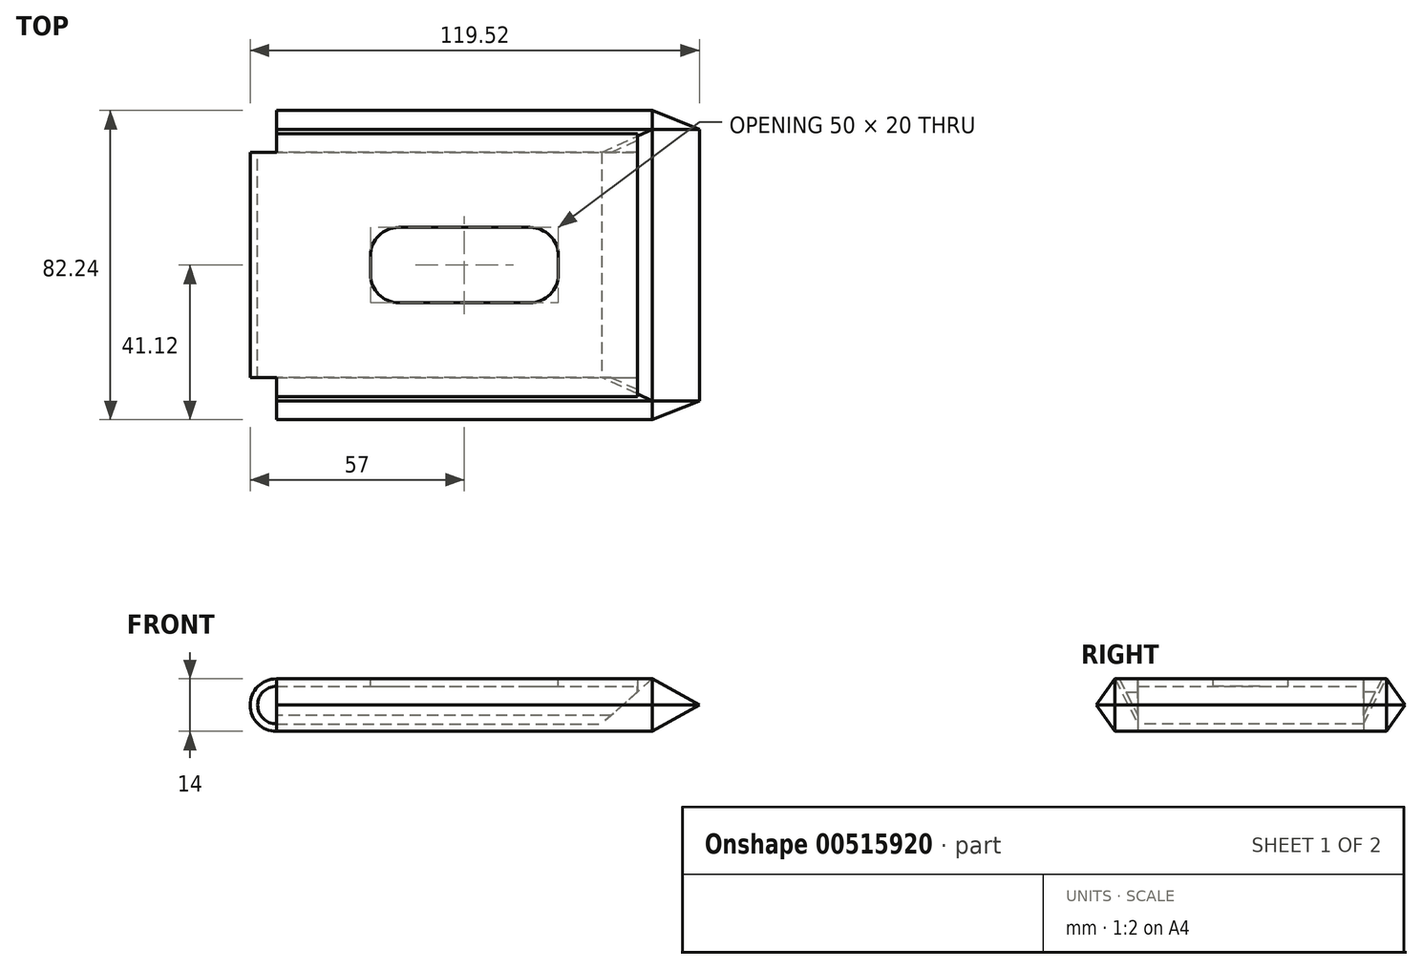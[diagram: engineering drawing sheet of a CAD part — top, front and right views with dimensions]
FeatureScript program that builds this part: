
annotation { "Feature Type Name" : "Feature", "Feature Type Description" : "" }
export const myFeature = defineFeature(function(context is Context, id is Id, definition is map)
    precondition{}
    {
        {
            var Q0;
            Q0=qCreatedBy(makeId("Front.planeOp"),FACE);
            var sketch = newSketch(context, id + "F0", { "sketchPlane" : qUnion([Q0])});
            skArc(sketch, "E0", {"start": v(0, 5) * mm, "mid": v(-5, 0) * mm, "end": v(0, -5) * mm});
            skLineSegment(sketch, "E1", {"start": v(0, 5) * mm, "end": v(100, 5) * mm});
            skLineSegment(sketch, "E2", {"start": v(0, -5) * mm, "end": v(100, -5) * mm});
            skLineSegment(sketch, "E3.0", {"start": v(0, 7) * mm, "end": v(100, 7) * mm});
            skArc(sketch, "E3.1", {"start": v(0, 7) * mm, "mid": v(-7, 0) * mm, "end": v(0, -7) * mm});
            skLineSegment(sketch, "E3.2", {"start": v(0, -7) * mm, "end": v(100, -7) * mm});
            skLineSegment(sketch, "E4", {"start": v(100, 7) * mm, "end": v(100, 5) * mm});
            skLineSegment(sketch, "E5", {"start": v(100, -5) * mm, "end": v(100, -7) * mm});
            skSolve(sketch);
        }
        {
            var Q0;
            Q0 = qSketchRegion(id + "F0", true);
            extrude(context, id + "F1", {"entities" : qUnion([Q0]), "depth" : 60 * mm, "offsetDistance" : 25 * mm});
        }
        {
            var Q0;
            Q0=makeQuery(id+"F1.opExtrude","SWEPT_FACE",FACE,{"disambiguationData":[OSD([sQuery(id+"F0.wireOp",EDGE,"E3.0")])]});
            var sketch = newSketch(context, id + "F2", { "sketchPlane" : qUnion([Q0])});
            skLineSegment(sketch, "E6", {"start": v(50, 0) * mm, "end": v(50, -60) * mm, "construction": true});
            skLineSegment(sketch, "E7.bottom", {"start": v(67.5, -40) * mm, "end": v(32.5, -40) * mm});
            skLineSegment(sketch, "E7.top", {"start": v(67.5, -20) * mm, "end": v(32.5, -20) * mm});
            skLineSegment(sketch, "E7.left", {"start": v(75, -32.5) * mm, "end": v(75, -27.5) * mm});
            skLineSegment(sketch, "E7.right", {"start": v(25, -32.5) * mm, "end": v(25, -27.5) * mm});
            skPoint(sketch, "E7.middle", {"position": v(50, -30) * mm});
            skPoint(sketch, "E8.visualSharp", {"position": v(25, -20) * mm});
            skArc(sketch, "E8.filletArc", {"start": v(32.5, -20) * mm, "mid": v(27.2, -22.2) * mm, "end": v(25, -27.5) * mm});
            skPoint(sketch, "E9.visualSharp", {"position": v(25, -40) * mm});
            skArc(sketch, "E9.filletArc", {"start": v(25, -32.5) * mm, "mid": v(27.2, -37.8) * mm, "end": v(32.5, -40) * mm});
            skPoint(sketch, "E10.visualSharp", {"position": v(75, -40) * mm});
            skArc(sketch, "E10.filletArc", {"start": v(67.5, -40) * mm, "mid": v(72.8, -37.8) * mm, "end": v(75, -32.5) * mm});
            skPoint(sketch, "E11.visualSharp", {"position": v(75, -20) * mm});
            skArc(sketch, "E11.filletArc", {"start": v(75, -27.5) * mm, "mid": v(72.8, -22.2) * mm, "end": v(67.5, -20) * mm});
            skSolve(sketch);
        }
        {
            var Q0;
            Q0 = qSketchRegion(id + "F2", true);
            var Q1;
            Q1=makeQuery(id+"F1.opExtrude","SWEPT_FACE",FACE,{"disambiguationData":[OSD([sQuery(id+"F0.wireOp",EDGE,"E1")])]});
            extrude(context, id + "F3", {"entities" : qUnion([Q0]), "operationType" : NewBodyOperationType.REMOVE, "endBound" : BoundingType.UP_TO_SURFACE, "oppositeDirection" : true, "depth" : 25 * mm, "endBoundEntityFace" : qUnion([Q1]), "offsetDistance" : 25 * mm});
        }
        {
            var Q0;
            Q0=qCreatedBy(makeId("Right.planeOp"),FACE);
            var sketch = newSketch(context, id + "F4", { "sketchPlane" : qUnion([Q0])});
            skLineSegment(sketch, "E12", {"start": v(-60, 7) * mm, "end": v(-65, 7) * mm});
            skLineSegment(sketch, "E13", {"start": v(-65, 7) * mm, "end": v(-60, -2.8) * mm});
            skLineSegment(sketch, "E14", {"start": v(-60, -2.8) * mm, "end": v(-60, 7) * mm});
            skLineSegment(sketch, "E15", {"start": v(-60, -7) * mm, "end": v(-66.12, -7) * mm});
            skLineSegment(sketch, "E16", {"start": v(-66.12, -7) * mm, "end": v(-71.12, 0) * mm});
            skLineSegment(sketch, "E17", {"start": v(-71.12, 0) * mm, "end": v(-66.12, 7) * mm});
            skLineSegment(sketch, "E18", {"start": v(-66.12, 7) * mm, "end": v(-60, -5) * mm});
            skLineSegment(sketch, "E19", {"start": v(-60, -5) * mm, "end": v(-60, -7) * mm});
            skLineSegment(sketch, "E20", {"start": v(-65, 7) * mm, "end": v(-66.12, 7) * mm, "construction": true});
            skLineSegment(sketch, "E21", {"start": v(-66.12, 7) * mm, "end": v(-66.12, -7) * mm, "construction": true});
            skLineSegment(sketch, "E22", {"start": v(-30, 6.94) * mm, "end": v(-30, -7) * mm, "construction": true});
            skLineSegment(sketch, "E23.MirrorCS", {"start": v(0, 7) * mm, "end": v(5, 7) * mm});
            skLineSegment(sketch, "E24.MirrorCS", {"start": v(0, -2.8) * mm, "end": v(0, 7) * mm});
            skLineSegment(sketch, "E25.MirrorCS", {"start": v(5, 7) * mm, "end": v(0, -2.8) * mm});
            skLineSegment(sketch, "E26.MirrorCS", {"start": v(11.12, 0) * mm, "end": v(6.12, 7) * mm});
            skLineSegment(sketch, "E27.MirrorCS", {"start": v(6.12, 7) * mm, "end": v(0, -5) * mm});
            skLineSegment(sketch, "E28.MirrorCS", {"start": v(0, -5) * mm, "end": v(0, -7) * mm});
            skLineSegment(sketch, "E29.MirrorCS", {"start": v(0, -7) * mm, "end": v(6.12, -7) * mm});
            skLineSegment(sketch, "E30.MirrorCS", {"start": v(6.12, -7) * mm, "end": v(11.12, 0) * mm});
            skLineSegment(sketch, "E31", {"start": v(-66.12, 0) * mm, "end": v(-71.12, 0) * mm, "construction": true});
            skSolve(sketch);
        }
        {
            var Q0;
            Q0=makeQuery(id+"F4.imprint","IMPRINT",FACE,{"disambiguationData":[TD([[makeQuery(id+"F4.imprint","IMPRINT",EDGE,{"derivedFrom":sQuery(id+"F4.wireOp",EDGE,"E12")}),1.0]])]});
            var Q1;
            Q1=makeQuery(id+"F4.imprint","IMPRINT",FACE,{"disambiguationData":[TD([[makeQuery(id+"F4.imprint","IMPRINT",EDGE,{"derivedFrom":sQuery(id+"F4.wireOp",EDGE,"E15")}),-1.0]])]});
            var Q2;
            Q2=makeQuery(id+"F4.imprint","IMPRINT",FACE,{"disambiguationData":[TD([[makeQuery(id+"F4.imprint","IMPRINT",EDGE,{"derivedFrom":sQuery(id+"F4.wireOp",EDGE,"E23.MirrorCS")}),-1.0]])]});
            var Q3;
            Q3=makeQuery(id+"F4.imprint","IMPRINT",FACE,{"disambiguationData":[TD([[makeQuery(id+"F4.imprint","IMPRINT",EDGE,{"derivedFrom":sQuery(id+"F4.wireOp",EDGE,"E26.MirrorCS")}),1.0]])]});
            var Q4;
            Q4=makeQuery(id+"F1.opExtrude","SWEPT_FACE",FACE,{"disambiguationData":[OSD([sQuery(id+"F0.wireOp",EDGE,"E4")])]});
            extrude(context, id + "F5", {"entities" : qUnion([Q0, Q1, Q2, Q3]), "operationType" : NewBodyOperationType.ADD, "endBound" : BoundingType.UP_TO_SURFACE, "depth" : 25 * mm, "endBoundEntityFace" : qUnion([Q4]), "offsetDistance" : 25 * mm});
        }
        {
            var Q0;
            Q0=makeQuery(id+"F5.boolean.opBoolean","MERGE",FACE,{"derivedFrom":[makeQuery(id+"F1.opExtrude","SWEPT_FACE",FACE,{"disambiguationData":[OSD([sQuery(id+"F0.wireOp",EDGE,"E4")])]}),makeQuery(id+"F5.opExtrude","CAP_FACE",FACE,{"disambiguationData":[OSD([sQuery(id+"F4.wireOp",EDGE,"E12"),sQuery(id+"F4.wireOp",EDGE,"E13"),sQuery(id+"F4.wireOp",EDGE,"E14")])],"isStart":false}),makeQuery(id+"F5.opExtrude","CAP_FACE",FACE,{"disambiguationData":[OSD([sQuery(id+"F4.wireOp",EDGE,"E23.MirrorCS"),sQuery(id+"F4.wireOp",EDGE,"E24.MirrorCS"),sQuery(id+"F4.wireOp",EDGE,"E25.MirrorCS")])],"isStart":false})]});
            extrude(context, id + "F6", {"entities" : qUnion([Q0]), "operationType" : NewBodyOperationType.REMOVE, "oppositeDirection" : true, "depth" : 4 * mm, "offsetDistance" : 25 * mm});
        }
        {
            var Q0;
            Q0=makeQuery(id+"F5.opExtrude","SWEPT_FACE",FACE,{"disambiguationData":[OSD([sQuery(id+"F4.wireOp",EDGE,"E24.MirrorCS")])]});
            var Q1;
            Q1=makeQuery(id+"F5.opExtrude","SWEPT_FACE",FACE,{"disambiguationData":[OSD([sQuery(id+"F4.wireOp",EDGE,"E14")])]});
            cPlane(context, id + "F7", {"entities" : qUnion([Q0, Q1]), "cplaneType" : CPlaneType.MID_PLANE, "offset" : 25 * mm, "width" : 150 * mm, "height" : 150 * mm});
        }
        {
            var Q0;
            Q0=qCreatedBy(id+"F7.planeOp",FACE);
            var sketch = newSketch(context, id + "F8", { "sketchPlane" : qUnion([Q0])});
            skLineSegment(sketch, "E32", {"start": v(100, -5) * mm, "end": v(100, -7) * mm});
            skLineSegment(sketch, "E33", {"start": v(112.52, 0) * mm, "end": v(100, 7) * mm});
            skLineSegment(sketch, "E34", {"start": v(100, 7) * mm, "end": v(86.56, -5) * mm});
            skLineSegment(sketch, "E35", {"start": v(86.56, -5) * mm, "end": v(100, -5) * mm});
            skLineSegment(sketch, "E36", {"start": v(100, -7) * mm, "end": v(112.52, 0) * mm});
            skLineSegment(sketch, "E37", {"start": v(100, 7) * mm, "end": v(100, -7) * mm, "construction": true});
            skLineSegment(sketch, "E38", {"start": v(100, 0) * mm, "end": v(112.52, 0) * mm, "construction": true});
            skLineSegment(sketch, "E39", {"start": v(100, 7) * mm, "end": v(100, 7) * mm});
            skSolve(sketch);
        }
        {
            var Q0;
            Q0 = qSketchRegion(id + "F8", true);
            var Q1;
            Q1=makeQuery(id+"F5.opExtrude","CAP_VERTEX",VERTEX,{"disambiguationData":[OSD([sQuery(id+"F4.wireOp",EDGE,"E29.MirrorCS"),sQuery(id+"F4.wireOp",EDGE,"E30.MirrorCS")])],"isStart":false});
            var Q2;
            Q2=makeQuery(id+"F5.opExtrude","CAP_VERTEX",VERTEX,{"disambiguationData":[OSD([sQuery(id+"F4.wireOp",EDGE,"E15"),sQuery(id+"F4.wireOp",EDGE,"E16")])],"isStart":false});
            extrude(context, id + "F9", {"entities" : qUnion([Q0]), "operationType" : NewBodyOperationType.ADD, "endBound" : BoundingType.UP_TO_VERTEX, "oppositeDirection" : true, "depth" : 25 * mm, "endBoundEntityVertex" : qUnion([Q1]), "offsetDistance" : 25 * mm});
        }
        {
            var Q0;
            Q0=makeQuery(id+"F9.opExtrude","CAP_FACE",FACE,{"disambiguationData":[OSD([sQuery(id+"F8.wireOp",EDGE,"E32"),sQuery(id+"F8.wireOp",EDGE,"E33"),sQuery(id+"F8.wireOp",EDGE,"E34"),sQuery(id+"F8.wireOp",EDGE,"E35"),sQuery(id+"F8.wireOp",EDGE,"E36")])],"isStart":true});
            var Q1;
            Q1=makeQuery(id+"F5.opExtrude","CAP_VERTEX",VERTEX,{"disambiguationData":[OSD([sQuery(id+"F4.wireOp",EDGE,"E15"),sQuery(id+"F4.wireOp",EDGE,"E16")])],"isStart":false});
            extrude(context, id + "F10", {"entities" : qUnion([Q0]), "operationType" : NewBodyOperationType.ADD, "endBound" : BoundingType.UP_TO_VERTEX, "depth" : 25 * mm, "endBoundEntityVertex" : qUnion([Q1]), "offsetDistance" : 25 * mm});
        }
        {
            var Q1;
            {var subQ0=sQuery(id+"F4.wireOp",EDGE,"E16");var subQ1=sQuery(id+"F4.wireOp",EDGE,"E15");var subQ3=sQuery(id+"F4.wireOp",EDGE,"E17");var subQ4=sQuery(id+"F4.wireOp",EDGE,"E18");var subQ5=sQuery(id+"F4.wireOp",EDGE,"E29.MirrorCS");Q1=makeQuery(id+"F9.boolean.opBoolean","SPLIT",FACE,{"disambiguationData":[TD([makeQuery(id+"F1.opExtrude","SWEPT_FACE",FACE,{"disambiguationData":[OSD([sQuery(id+"F0.wireOp",EDGE,"E2")])]})])],"derivedFrom":makeQuery(id+"F5.boolean.opBoolean","MERGE",FACE,{"derivedFrom":[makeQuery(id+"F1.opExtrude","SWEPT_FACE",FACE,{"disambiguationData":[OSD([sQuery(id+"F0.wireOp",EDGE,"E5")])]}),makeQuery(id+"F5.opExtrude","CAP_FACE",FACE,{"disambiguationData":[OSD([subQ1,subQ0,subQ3,subQ4,sQuery(id+"F4.wireOp",EDGE,"E19")])],"isStart":false}),makeQuery(id+"F5.opExtrude","CAP_FACE",FACE,{"disambiguationData":[OSD([sQuery(id+"F4.wireOp",EDGE,"E26.MirrorCS"),sQuery(id+"F4.wireOp",EDGE,"E27.MirrorCS"),sQuery(id+"F4.wireOp",EDGE,"E28.MirrorCS"),subQ5,sQuery(id+"F4.wireOp",EDGE,"E30.MirrorCS")])],"isStart":false})]})});}
            var Q2;
            Q2=makeQuery(id+"F10.opExtrude","CAP_FACE",FACE,{"disambiguationData":[OSD([sQuery(id+"F8.wireOp",EDGE,"E32"),sQuery(id+"F8.wireOp",EDGE,"E33"),sQuery(id+"F8.wireOp",EDGE,"E34"),sQuery(id+"F8.wireOp",EDGE,"E35"),sQuery(id+"F8.wireOp",EDGE,"E36")])],"isStart":false});
            loft(context, id + "F11", {"operationType" : NewBodyOperationType.ADD, "sheetProfilesArray" : [{ "sheetProfileEntities" : qUnion([Q1]) }, { "sheetProfileEntities" : qUnion([Q2]) }]});
        }
        {
            var Q1;
            Q1=makeQuery(id+"F9.opExtrude","CAP_FACE",FACE,{"disambiguationData":[OSD([sQuery(id+"F8.wireOp",EDGE,"E32"),sQuery(id+"F8.wireOp",EDGE,"E33"),sQuery(id+"F8.wireOp",EDGE,"E34"),sQuery(id+"F8.wireOp",EDGE,"E35"),sQuery(id+"F8.wireOp",EDGE,"E36")])],"isStart":false});
            var Q2;
            {var subQ0=sQuery(id+"F4.wireOp",EDGE,"E26.MirrorCS");var subQ1=sQuery(id+"F4.wireOp",EDGE,"E27.MirrorCS");var subQ2=sQuery(id+"F4.wireOp",EDGE,"E15");var subQ4=sQuery(id+"F4.wireOp",EDGE,"E29.MirrorCS");var subQ5=sQuery(id+"F4.wireOp",EDGE,"E30.MirrorCS");Q2=makeQuery(id+"F9.boolean.opBoolean","SPLIT",FACE,{"disambiguationData":[TD([makeQuery(id+"F5.opExtrude","SWEPT_FACE",FACE,{"disambiguationData":[OSD([subQ0])]})])],"derivedFrom":makeQuery(id+"F5.boolean.opBoolean","MERGE",FACE,{"derivedFrom":[makeQuery(id+"F1.opExtrude","SWEPT_FACE",FACE,{"disambiguationData":[OSD([sQuery(id+"F0.wireOp",EDGE,"E5")])]}),makeQuery(id+"F5.opExtrude","CAP_FACE",FACE,{"disambiguationData":[OSD([subQ2,sQuery(id+"F4.wireOp",EDGE,"E16"),sQuery(id+"F4.wireOp",EDGE,"E17"),sQuery(id+"F4.wireOp",EDGE,"E18"),sQuery(id+"F4.wireOp",EDGE,"E19")])],"isStart":false}),makeQuery(id+"F5.opExtrude","CAP_FACE",FACE,{"disambiguationData":[OSD([subQ0,subQ1,sQuery(id+"F4.wireOp",EDGE,"E28.MirrorCS"),subQ4,subQ5])],"isStart":false})]})});}
            loft(context, id + "F12", {"operationType" : NewBodyOperationType.ADD, "sheetProfilesArray" : [{ "sheetProfileEntities" : qUnion([Q1]) }, { "sheetProfileEntities" : qUnion([Q2]) }]});
        }
    });
